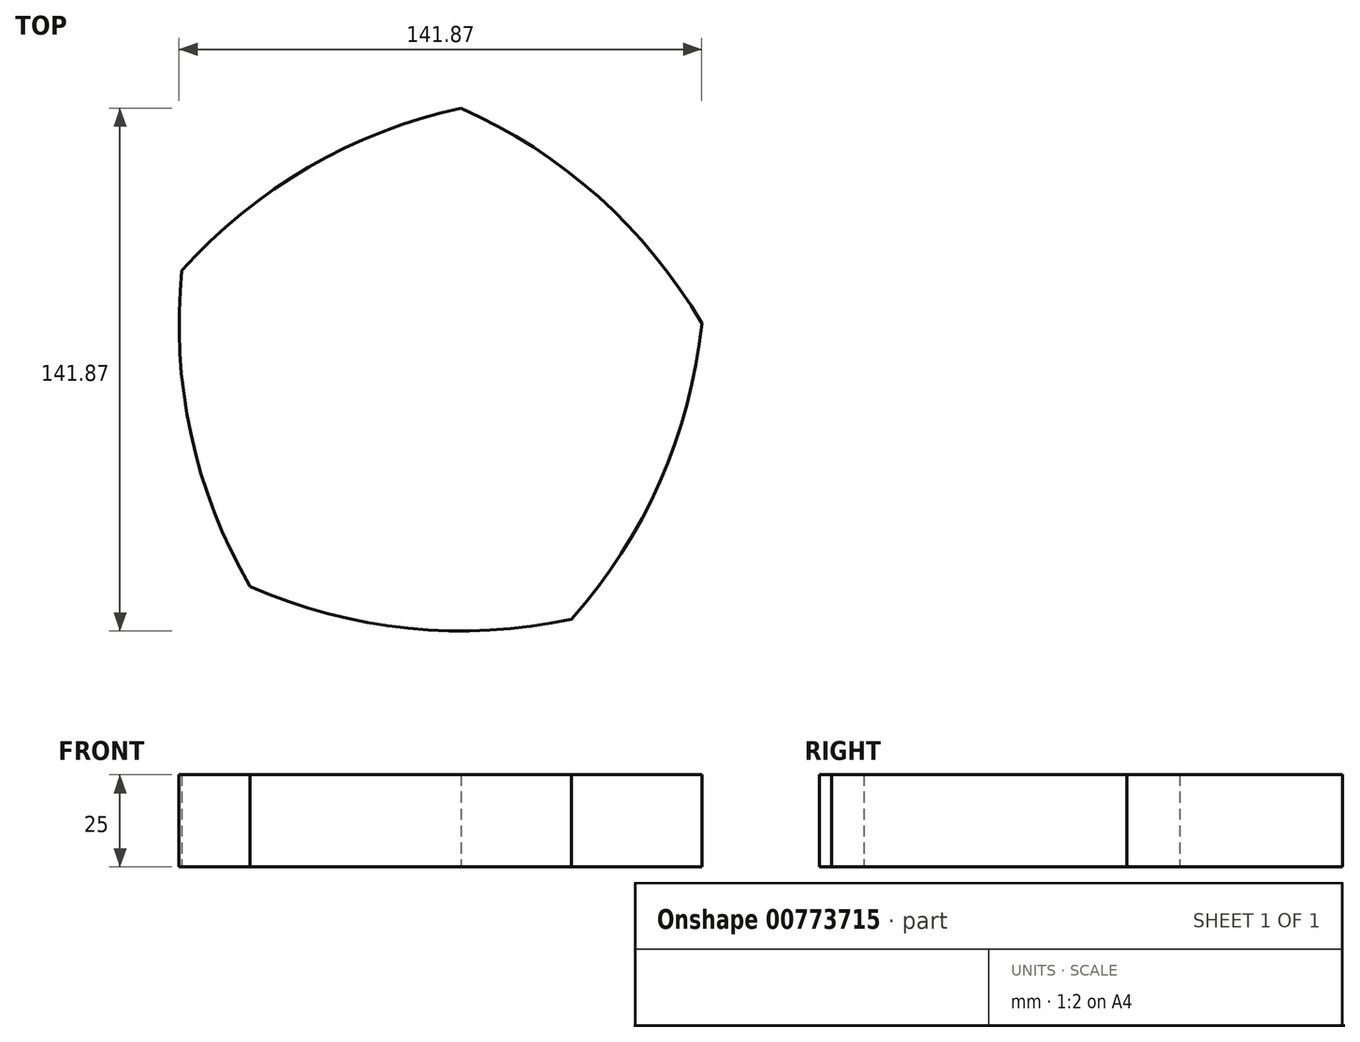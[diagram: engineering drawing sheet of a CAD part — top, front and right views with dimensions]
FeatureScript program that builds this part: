
annotation { "Feature Type Name" : "Feature", "Feature Type Description" : "" }
export const myFeature = defineFeature(function(context is Context, id is Id, definition is map)
    precondition{}
    {
        {
            var Q0;
            Q0=qCreatedBy(makeId("Top.planeOp"),FACE);
            var sketch = newSketch(context, id + "F0", { "sketchPlane" : qUnion([Q0])});
            skPoint(sketch, "E0.0.midPoint", {"position": v(-30.35, 52.15) * mm});
            skCircle(sketch, "E1", {"center": v(7.54, 74.2) * mm, "radius": 141.87 * mm});
            skCircle(sketch, "E2", {"center": v(-68.24, 30.1) * mm, "radius": 141.87 * mm});
            skCircle(sketch, "E3", {"center": v(-49.72, -55.6) * mm, "radius": 141.87 * mm});
            skCircle(sketch, "E4", {"center": v(37.52, -64.46) * mm, "radius": 141.87 * mm});
            skCircle(sketch, "E5", {"center": v(72.9, 15.76) * mm, "radius": 141.87 * mm});
            skSolve(sketch);
        }
        {
            var Q0;
            {var subQ3=sQuery(id+"F0.wireOp",EDGE,"E5");var subQ5=sQuery(id+"F0.wireOp",EDGE,"E1");var subQ6=makeQuery(id+"F0.imprint","INTERSECT",VERTEX,{"disambiguationData":[OD(1.0)],"derivedFrom":[subQ5,subQ3]});Q0=makeQuery(id+"F0.imprint","IMPRINT",FACE,{"disambiguationData":[TD([[makeQuery(id+"F0.imprint","IMPRINT",EDGE,{"disambiguationData":[TD([[subQ6,-1.0]])],"derivedFrom":subQ5}),1.0]])]});}
            extrude(context, id + "F1", {"entities" : qUnion([Q0]), "depth" : 25 * mm, "offsetDistance" : 25 * mm});
        }
    });
